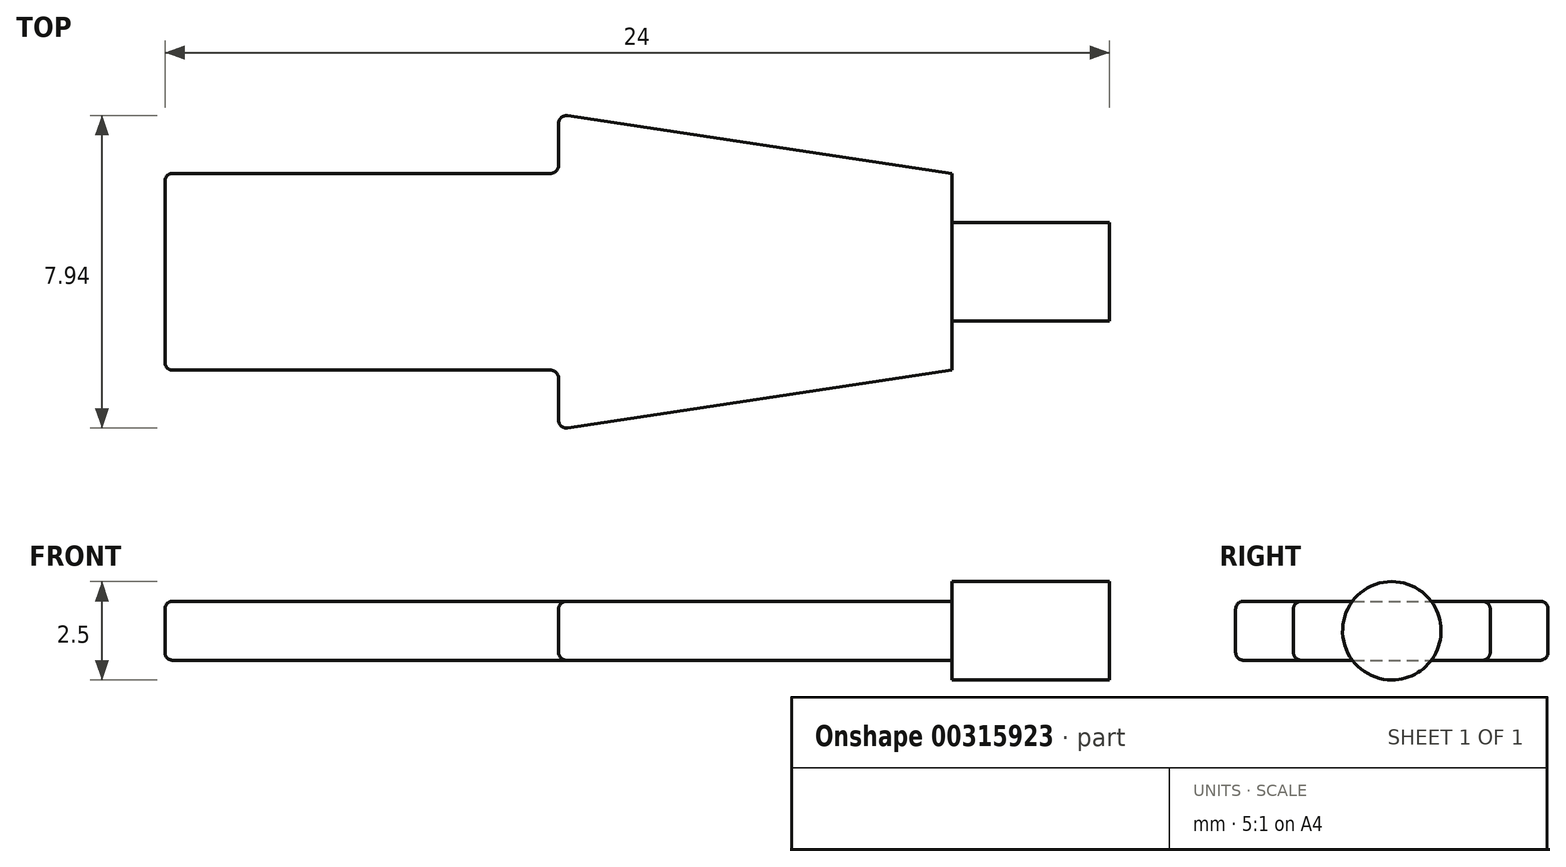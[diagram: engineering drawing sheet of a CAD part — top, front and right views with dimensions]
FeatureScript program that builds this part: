
annotation { "Feature Type Name" : "Feature", "Feature Type Description" : "" }
export const myFeature = defineFeature(function(context is Context, id is Id, definition is map)
    precondition{}
    {
        {
            var Q0;
            Q0=qCreatedBy(makeId("Top.planeOp"),FACE);
            var sketch = newSketch(context, id + "F0", { "sketchPlane" : qUnion([Q0])});
            skLineSegment(sketch, "E0", {"start": v(0, 0) * mm, "end": v(0, 2.5) * mm});
            skLineSegment(sketch, "E1", {"start": v(0, 2.5) * mm, "end": v(10, 2.5) * mm});
            skLineSegment(sketch, "E2", {"start": v(10, 2.5) * mm, "end": v(10, 4) * mm});
            skLineSegment(sketch, "E3", {"start": v(10, 4) * mm, "end": v(20, 2.5) * mm});
            skLineSegment(sketch, "E4", {"start": v(20, 2.5) * mm, "end": v(20, 0) * mm});
            skLineSegment(sketch, "E5", {"start": v(20, 0) * mm, "end": v(0, 0) * mm, "construction": true});
            skLineSegment(sketch, "E6.MirrorCS", {"start": v(20, -2.5) * mm, "end": v(20, 0) * mm});
            skLineSegment(sketch, "E7.MirrorCS", {"start": v(10, -4) * mm, "end": v(20, -2.5) * mm});
            skLineSegment(sketch, "E8.MirrorCS", {"start": v(10, -2.5) * mm, "end": v(10, -4) * mm});
            skLineSegment(sketch, "E9.MirrorCS", {"start": v(0, 0) * mm, "end": v(0, -2.5) * mm});
            skLineSegment(sketch, "E10.MirrorCS", {"start": v(0, -2.5) * mm, "end": v(10, -2.5) * mm});
            skSolve(sketch);
        }
        {
            var Q0;
            Q0=makeQuery(id+"F0.imprint","IMPRINT",FACE,{"disambiguationData":[TD([[makeQuery(id+"F0.imprint","IMPRINT",EDGE,{"derivedFrom":sQuery(id+"F0.wireOp",EDGE,"E0")}),-1.0]])]});
            extrude(context, id + "F1", {"entities" : qUnion([Q0]), "depth" : 1.5 * mm});
        }
        {
            var Q0;
            Q0=makeQuery(id+"F1.opExtrude","SWEPT_FACE",FACE,{"disambiguationData":[OSD([sQuery(id+"F0.wireOp",EDGE,"E4"),sQuery(id+"F0.wireOp",EDGE,"E6.MirrorCS")])]});
            var sketch = newSketch(context, id + "F2", { "sketchPlane" : qUnion([Q0])});
            skPoint(sketch, "E11.centerSnap0", {"position": v(0, 1.5) * mm});
            skLineSegment(sketch, "E12", {"start": v(-2.5, 0.75) * mm, "end": v(2.5, 0.75) * mm, "construction": true});
            skLineSegment(sketch, "E13", {"start": v(0, 1.5) * mm, "end": v(0, 0) * mm, "construction": true});
            skPoint(sketch, "E14", {"position": v(2.5, 0.75) * mm});
            skCircle(sketch, "E15", {"center": v(0, 0.75) * mm, "radius": 1.25 * mm});
            skSolve(sketch);
        }
        {
            var Q0;
            Q0 = qSketchRegion(id + "F2", true);
            var Q1;
            Q1=sQuery(id+"F2.wireOp",EDGE,"E15");
            extrude(context, id + "F3", {"entities" : qUnion([Q0]), "operationType" : NewBodyOperationType.ADD, "surfaceEntities" : qUnion([Q1]), "depth" : 4 * mm});
        }
        {
            var Q0;
            Q0=makeQuery(id+"F1.opExtrude","CAP_EDGE",EDGE,{"disambiguationData":[OSD([sQuery(id+"F0.wireOp",EDGE,"E10.MirrorCS")])],"isStart":false});
            var Q1;
            Q1=makeQuery(id+"F1.opExtrude","CAP_EDGE",EDGE,{"disambiguationData":[OSD([sQuery(id+"F0.wireOp",EDGE,"E0"),sQuery(id+"F0.wireOp",EDGE,"E9.MirrorCS")])],"isStart":false});
            var Q2;
            Q2=makeQuery(id+"F1.opExtrude","CAP_EDGE",EDGE,{"disambiguationData":[OSD([sQuery(id+"F0.wireOp",EDGE,"E1")])],"isStart":false});
            var Q3;
            Q3=makeQuery(id+"F1.opExtrude","CAP_EDGE",EDGE,{"disambiguationData":[OSD([sQuery(id+"F0.wireOp",EDGE,"E3")])],"isStart":false});
            var Q4;
            Q4=makeQuery(id+"F1.opExtrude","CAP_EDGE",EDGE,{"disambiguationData":[OSD([sQuery(id+"F0.wireOp",EDGE,"E7.MirrorCS")])],"isStart":false});
            var Q5;
            Q5=makeQuery(id+"F1.opExtrude","CAP_EDGE",EDGE,{"disambiguationData":[OSD([sQuery(id+"F0.wireOp",EDGE,"E8.MirrorCS")])],"isStart":false});
            var Q6;
            Q6=makeQuery(id+"F1.opExtrude","CAP_EDGE",EDGE,{"disambiguationData":[OSD([sQuery(id+"F0.wireOp",EDGE,"E2")])],"isStart":false});
            var Q7;
            Q7=makeQuery(id+"F1.opExtrude","CAP_EDGE",EDGE,{"disambiguationData":[OSD([sQuery(id+"F0.wireOp",EDGE,"E8.MirrorCS")])],"isStart":true});
            var Q8;
            Q8=makeQuery(id+"F1.opExtrude","CAP_EDGE",EDGE,{"disambiguationData":[OSD([sQuery(id+"F0.wireOp",EDGE,"E7.MirrorCS")])],"isStart":true});
            var Q9;
            Q9=makeQuery(id+"F1.opExtrude","CAP_EDGE",EDGE,{"disambiguationData":[OSD([sQuery(id+"F0.wireOp",EDGE,"E10.MirrorCS")])],"isStart":true});
            var Q10;
            Q10=makeQuery(id+"F1.opExtrude","CAP_EDGE",EDGE,{"disambiguationData":[OSD([sQuery(id+"F0.wireOp",EDGE,"E0"),sQuery(id+"F0.wireOp",EDGE,"E9.MirrorCS")])],"isStart":true});
            var Q11;
            Q11=makeQuery(id+"F1.opExtrude","CAP_EDGE",EDGE,{"disambiguationData":[OSD([sQuery(id+"F0.wireOp",EDGE,"E2")])],"isStart":true});
            var Q12;
            Q12=makeQuery(id+"F1.opExtrude","CAP_EDGE",EDGE,{"disambiguationData":[OSD([sQuery(id+"F0.wireOp",EDGE,"E1")])],"isStart":true});
            var Q13;
            Q13=makeQuery(id+"F1.opExtrude","CAP_EDGE",EDGE,{"disambiguationData":[OSD([sQuery(id+"F0.wireOp",EDGE,"E3")])],"isStart":true});
            var Q14;
            Q14=makeQuery(id+"F1.opExtrude","SWEPT_EDGE",EDGE,{"disambiguationData":[OSD([sQuery(id+"F0.wireOp",EDGE,"E2"),sQuery(id+"F0.wireOp",EDGE,"E3")])]});
            var Q15;
            Q15=makeQuery(id+"F1.opExtrude","SWEPT_EDGE",EDGE,{"disambiguationData":[OSD([sQuery(id+"F0.wireOp",EDGE,"E1"),sQuery(id+"F0.wireOp",EDGE,"E2")])]});
            var Q16;
            Q16=makeQuery(id+"F1.opExtrude","SWEPT_EDGE",EDGE,{"disambiguationData":[OSD([sQuery(id+"F0.wireOp",EDGE,"E8.MirrorCS"),sQuery(id+"F0.wireOp",EDGE,"E10.MirrorCS")])]});
            var Q17;
            Q17=makeQuery(id+"F1.opExtrude","SWEPT_EDGE",EDGE,{"disambiguationData":[OSD([sQuery(id+"F0.wireOp",EDGE,"E7.MirrorCS"),sQuery(id+"F0.wireOp",EDGE,"E8.MirrorCS")])]});
            var Q18;
            Q18=makeQuery(id+"F1.opExtrude","SWEPT_EDGE",EDGE,{"disambiguationData":[OSD([sQuery(id+"F0.wireOp",EDGE,"E9.MirrorCS"),sQuery(id+"F0.wireOp",EDGE,"E10.MirrorCS")])]});
            var Q19;
            Q19=makeQuery(id+"F1.opExtrude","SWEPT_EDGE",EDGE,{"disambiguationData":[OSD([sQuery(id+"F0.wireOp",EDGE,"E0"),sQuery(id+"F0.wireOp",EDGE,"E1")])]});
            fillet(context, id + "F4", {"entities" : qUnion([Q0, Q1, Q2, Q3, Q4, Q5, Q6, Q7, Q8, Q9, Q10, Q11, Q12, Q13, Q14, Q15, Q16, Q17, Q18, Q19]), "radius" : .2 * mm, "tangentPropagation" : true, "allowEdgeOverflow" : false});
        }
    });
